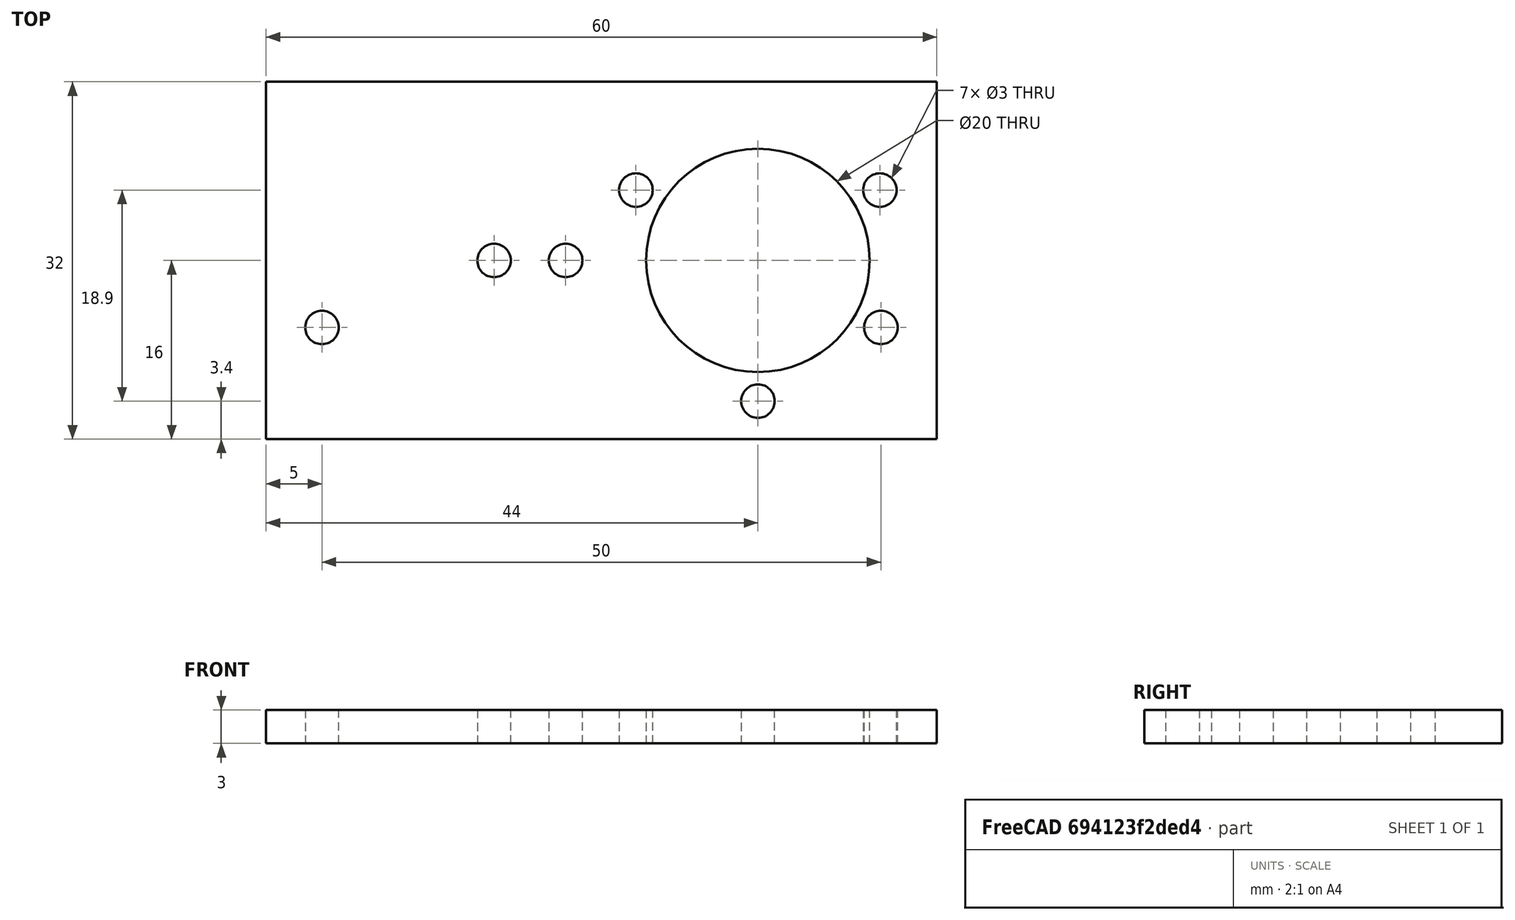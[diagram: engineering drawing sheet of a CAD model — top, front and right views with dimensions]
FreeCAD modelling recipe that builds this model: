
FCSTD DOCUMENT  (FreeCAD 0.16R6707 (Git))
Label: support_bas
License: All rights reserved
LicenseURL: http://en.wikipedia.org/wiki/All_rights_reserved
objects: Sketcher::SketchObject×1, PartDesign::Pad×1, Drawing::FeatureViewPart×1, Drawing::FeaturePage×1
note: 3 computed .brp shape members not serialized (recipe doc carries the construction recipe); baked Part::Feature solids carry a one-line shape summary decoded from their .brp

FEATURE [Sketcher::SketchObject] Sketch
  sketch-geometry (21):
    g0: LineSegment StartX=0 StartY=0 StartZ=0 EndX=60 EndY=0 EndZ=0
    g1: LineSegment StartX=60 StartY=0 StartZ=0 EndX=60 EndY=32 EndZ=0
    g2: LineSegment StartX=60 StartY=32 StartZ=0 EndX=0 EndY=32 EndZ=0
    g3: LineSegment StartX=0 StartY=32 StartZ=0 EndX=0 EndY=0 EndZ=0
    g4: GeomPoint [constr] X=44 Y=16 Z=0
    g5: GeomPoint [constr] X=55 Y=10 Z=0
    g6: GeomPoint [constr] X=44 Y=3.4 Z=0
    g7: GeomPoint [constr] X=54.9119 Y=22.3 Z=0
    g8: GeomPoint [constr] X=33.0881 Y=22.3 Z=0
    g9: Circle CenterX=33.0881 CenterY=22.3 CenterZ=0 NormalX=0 NormalY=0 NormalZ=1 Radius=1.5
    g10: Circle CenterX=54.9119 CenterY=22.3 CenterZ=0 NormalX=0 NormalY=0 NormalZ=1 Radius=1.5
    g11: Circle CenterX=44 CenterY=3.4 CenterZ=0 NormalX=0 NormalY=0 NormalZ=1 Radius=1.5
    g12: Circle CenterX=55 CenterY=10 CenterZ=0 NormalX=0 NormalY=0 NormalZ=1 Radius=1.5
    g13: GeomPoint [constr] X=5 Y=10 Z=0
    g14: Circle CenterX=5 CenterY=10 CenterZ=0 NormalX=0 NormalY=0 NormalZ=1 Radius=1.5
    g15: Circle CenterX=44 CenterY=16 CenterZ=0 NormalX=0 NormalY=0 NormalZ=1 Radius=10
    g16: Circle CenterX=20.4 CenterY=16 CenterZ=0 NormalX=0 NormalY=0 NormalZ=1 Radius=1.5
    g17: Circle CenterX=26.8 CenterY=16 CenterZ=0 NormalX=0 NormalY=0 NormalZ=1 Radius=1.5
    g18: GeomPoint [constr] X=46 Y=16 Z=0
    g19: GeomPoint [constr] X=39.6 Y=16 Z=0
    g20: GeomPoint [constr] X=33.2 Y=16 Z=0
  constraints (41):
    c: Coincident(g0,g1)
    c: Coincident(g1,g2)
    c: Coincident(g2,g3)
    c: Coincident(g3,g0)
    c: Horizontal(g0)
    c: Horizontal(g2)
    c: Vertical(g1)
    c: Vertical(g3)
    c: Coincident(g0,g-1)
    c: Distance(g3) = 32
    c: Distance(g2) = 60
    c: DistanceY(g4) = 16
    c: DistanceX(g4,g0) = 16
    c: DistanceX(g5,g0) = 5
    c: DistanceY(g5) = 10
    c: Coincident(g9,g8)
    c: Coincident(g10,g7)
    c: Coincident(g11,g6)
    c: Radius(g10) = 1.5
    c: Equal(g10,g9)
    c: Equal(g10,g11)
    c: Coincident(g12,g5)
    c: DistanceY(g13) = 10
    c: DistanceX(g13) = 5
    c: Coincident(g14,g13)
    c: Radius(g14) = 1.5
    c: Equal(g14,g12)
    c: Coincident(g15,g4)
    c: Radius(g15) = 10
    c: DistanceY(g17,g16) = 0
    c: DistanceX(g16,g17) = 6.4
    c: DistanceX(g18,g0) = 14
    c: DistanceY(g0,g18) = 16
    c: DistanceX(g19,g18) = 6.4
    c: DistanceX(g20,g19) = 6.4
    c: DistanceY(g19,g20) = 0
    c: DistanceY(g18,g19) = 0
    c: DistanceY(g20,g17) = 0
    c: DistanceX(g17,g20) = 6.4
    c: Radius(g16) = 1.5
    c: Equal(g16,g17)
FEATURE [PartDesign::Pad] Pad
  Length = 3
  Length2 = 100
  Sketch = -> Sketch
  Type = 0
FEATURE [Drawing::FeatureViewPart] Ortho  label="Ortho_0_0"
  Direction = (0,0,1)
  HiddenWidth = 0.15
  LineWidth = 0.35
  Rotation = 0
  ShowHiddenLines = false
  ShowSmoothLines = false
  Source = -> Pad
  Tolerance = 0.05
  ViewResult = <g id="Ortho_0_0"\n   transform="rotate(0,180,134.5) translate(180,134.5) scale(1,1)"\n  >\n<g   stroke="rgb(0, 0, 0)"\n   stroke-width="0.35"\n   stroke-linecap="butt"\n   stroke-linejoin="miter"\n   fill="none"\n   transform="scale(1,-1)"\n  >\n<path id= "1" d=" M 0 0 L 60 0 " />\n<path id= "2" d=" M 60 0 L 60 32 " />\n<path id= "3" d=" M 60 32 L 0 32 " />\n<path id= "4" d=" M 0 32 L 0 0 " />\n<circle cx ="44" cy ="16" r ="10" /><circle cx ="26.8" cy ="16" r ="1.5" /><circle cx ="20.4" cy ="16" r ="1.5" /><circle cx ="5" cy ="10" r ="1.5" /><circle cx ="55" cy ="10" r ="1.5" /><circle cx ="54.9119" cy ="22.3" r ="1.5" /><circle cx ="33.0881" cy ="22.3" r ="1.5" /><circle cx ="44" cy ="3.4" r ="1.5" /></g>\n</g>
  Visible = true
  X = 180
  Y = 134.5
FEATURE [Drawing::FeaturePage] Page
  EditableTexts = AUTHOR NAME | CREATION DATE | SUPERVISOR NAME | CHECK DATE | SCALE | WEIGHT | NUMBER | SHEET | TITLE | SUBTITLE
  Group = -> [Ortho]
